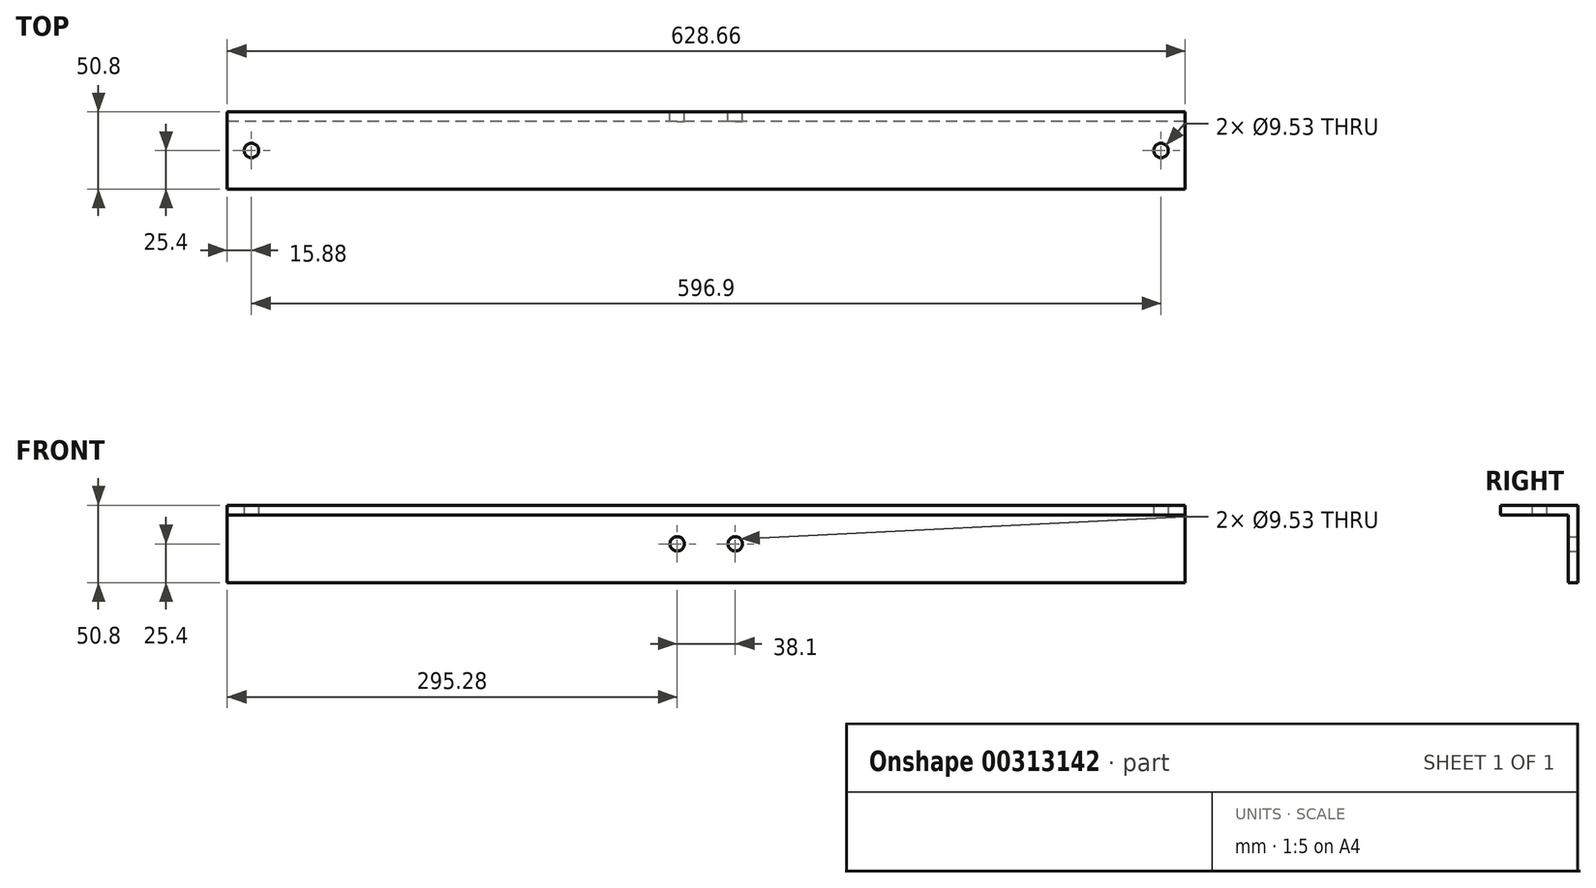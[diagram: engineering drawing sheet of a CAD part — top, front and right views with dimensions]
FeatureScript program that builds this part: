
annotation { "Feature Type Name" : "Feature", "Feature Type Description" : "" }
export const myFeature = defineFeature(function(context is Context, id is Id, definition is map)
    precondition{}
    {
        {
            var Q0;
            Q0=qCreatedBy(makeId("Right.planeOp"),FACE);
            var sketch = newSketch(context, id + "F0", { "sketchPlane" : qUnion([Q0])});
            skLineSegment(sketch, "E0", {"start": v(0, 0) * mm, "end": v(0, 44.45) * mm});
            skLineSegment(sketch, "E1", {"start": v(0, 44.45) * mm, "end": v(-44.45, 44.45) * mm});
            skLineSegment(sketch, "E2", {"start": v(-44.45, 44.45) * mm, "end": v(-44.45, 50.8) * mm});
            skLineSegment(sketch, "E3", {"start": v(-44.45, 50.8) * mm, "end": v(6.35, 50.8) * mm});
            skLineSegment(sketch, "E4", {"start": v(6.35, 50.8) * mm, "end": v(6.35, 0) * mm});
            skLineSegment(sketch, "E5", {"start": v(6.35, 0) * mm, "end": v(0, 0) * mm});
            skSolve(sketch);
        }
        {
            var Q0;
            Q0=qSketchRegion(id+"F0",true);
            extrude(context, id + "F1", {"entities" : qUnion([Q0]), "endBound" : BoundingType.SYMMETRIC, "depth" : 628.65 * mm});
        }
        {
            var Q0;
            Q0=makeQuery(id+"F1.opExtrude","SWEPT_FACE",FACE,{"disambiguationData":[OSD([sQuery(id+"F0.wireOp",EDGE,"E4")])]});
            var sketch = newSketch(context, id + "F2", { "sketchPlane" : qUnion([Q0])});
            skCircle(sketch, "E6", {"center": v(-19.05, 25.4) * mm, "radius": 4.76 * mm});
            skPoint(sketch, "E6.centerSnap0", {"position": v(-314.33, 25.4) * mm});
            skCircle(sketch, "E7", {"center": v(19.05, 25.4) * mm, "radius": 4.76 * mm});
            skLineSegment(sketch, "E8", {"start": v(-19.05, 25.4) * mm, "end": v(19.05, 25.4) * mm, "construction": true});
            skPoint(sketch, "E9", {"position": v(0, 25.4) * mm});
            skSolve(sketch);
        }
        {
            var Q0;
            Q0 = qSketchRegion(id + "F2", true);
            extrude(context, id + "F3", {"entities" : qUnion([Q0]), "operationType" : NewBodyOperationType.REMOVE, "endBound" : BoundingType.THROUGH_ALL, "oppositeDirection" : true, "depth" : 25.4 * mm});
        }
        {
            var Q0;
            Q0=makeQuery(id+"F1.opExtrude","SWEPT_FACE",FACE,{"disambiguationData":[OSD([sQuery(id+"F0.wireOp",EDGE,"E1")])]});
            var sketch = newSketch(context, id + "F4", { "sketchPlane" : qUnion([Q0])});
            skCircle(sketch, "E10", {"center": v(-298.45, 19.05) * mm, "radius": 4.76 * mm});
            skCircle(sketch, "E11", {"center": v(298.45, 19.05) * mm, "radius": 4.76 * mm});
            skSolve(sketch);
        }
        {
            var Q0;
            Q0 = qSketchRegion(id + "F4", true);
            extrude(context, id + "F5", {"entities" : qUnion([Q0]), "operationType" : NewBodyOperationType.REMOVE, "endBound" : BoundingType.THROUGH_ALL, "oppositeDirection" : true, "depth" : 25.4 * mm});
        }
    });
